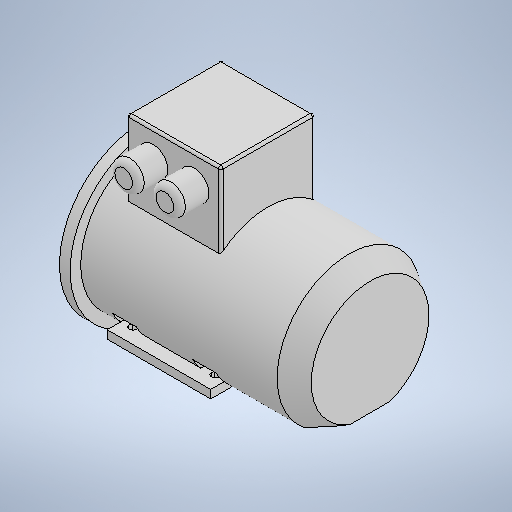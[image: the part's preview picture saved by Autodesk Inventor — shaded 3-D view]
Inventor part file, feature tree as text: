
AUTODESK INVENTOR PART (.ipt)
format: ipt  version: 2025.1 (Build 291241020, 241B)  size: 431,104 bytes
history: native  units: mm
features: sketch x7, extrude x6, projected_geometry x3, fillet x2, other x1, revolve x1, pattern_linear x1
ambient origin geometry x8: Origin, YZ Plane, XZ Plane, XY Plane, X Axis, Y Axis, Z Axis, Center Point
bodies: Body1 (feature_tree)
feature tree (21):
  other  "Твердое тело1"
  revolve  "Вращение1"
  extrude  "Выдавливание4"  Depth=9.0mm
  extrude  "Extrusion14"  TaperAngle=90.0deg  [1 undecoded]
  fillet  "Fillet1"  Radius=80.0mm
  fillet  "Fillet2"  Radius=18.0mm
  extrude  "Extrusion15"  Depth=122.0mm
  extrude  "Extrusion16"  Depth=18.0mm
  extrude  "Extrusion17"  Depth=10.0mm
  pattern_linear  "Rectangular Pattern2"  Spacing1=24.0mm  [1 undecoded]
  extrude  "Extrusion18"  Depth=10.0mm TaperAngle=0.0deg
  sketch  "Эскиз1"
  sketch  "Эскиз5"
  projected_geometry  "Спроецированная петля2"
  sketch  "Sketch15"  dims[d0=194.0mm d1=9.0mm]
  sketch  "Sketch16"  dims[d14=140.0mm d15=90.0deg d38=80.0mm d40=18.0mm]
  sketch  "Sketch17"  dims[d41=110.0mm d42=0.0mm d103=122.0mm]
  projected_geometry  "Projected Loop7"
  sketch  "Sketch18"  dims[d104=100.0mm d105=18.0mm]
  sketch  "Sketch19"  dims[d106=25.0mm d107=35.0mm d108=24.0mm d109=25.0mm d110=0.0mm d111=5.0mm d112=2.0mm d113=14.0mm d114=25.0mm d115=0.0mm d116=115.0mm d117=88.0mm d118=37.0mm d119=70.0mm d120=28.0mm d121=3.0mm d122=3.0mm d123=14.0mm d124=7.0mm d125=0.0mm d126=20.0mm d127=10.0mm d128=20.0mm d129=0.0mm d130=20.0mm d132=68.0mm d133=10.0mm d134=0.0mm d76=0.5mm d77=0.872665mm d78=0.5mm d79=0.872665mm]
  projected_geometry  "Projected Loop8"
note: 2 required parameter values undecoded (feature->parameter linkage not recoverable at this tier; creation-order binding heuristic only, values carry confidence <= 0.55)
